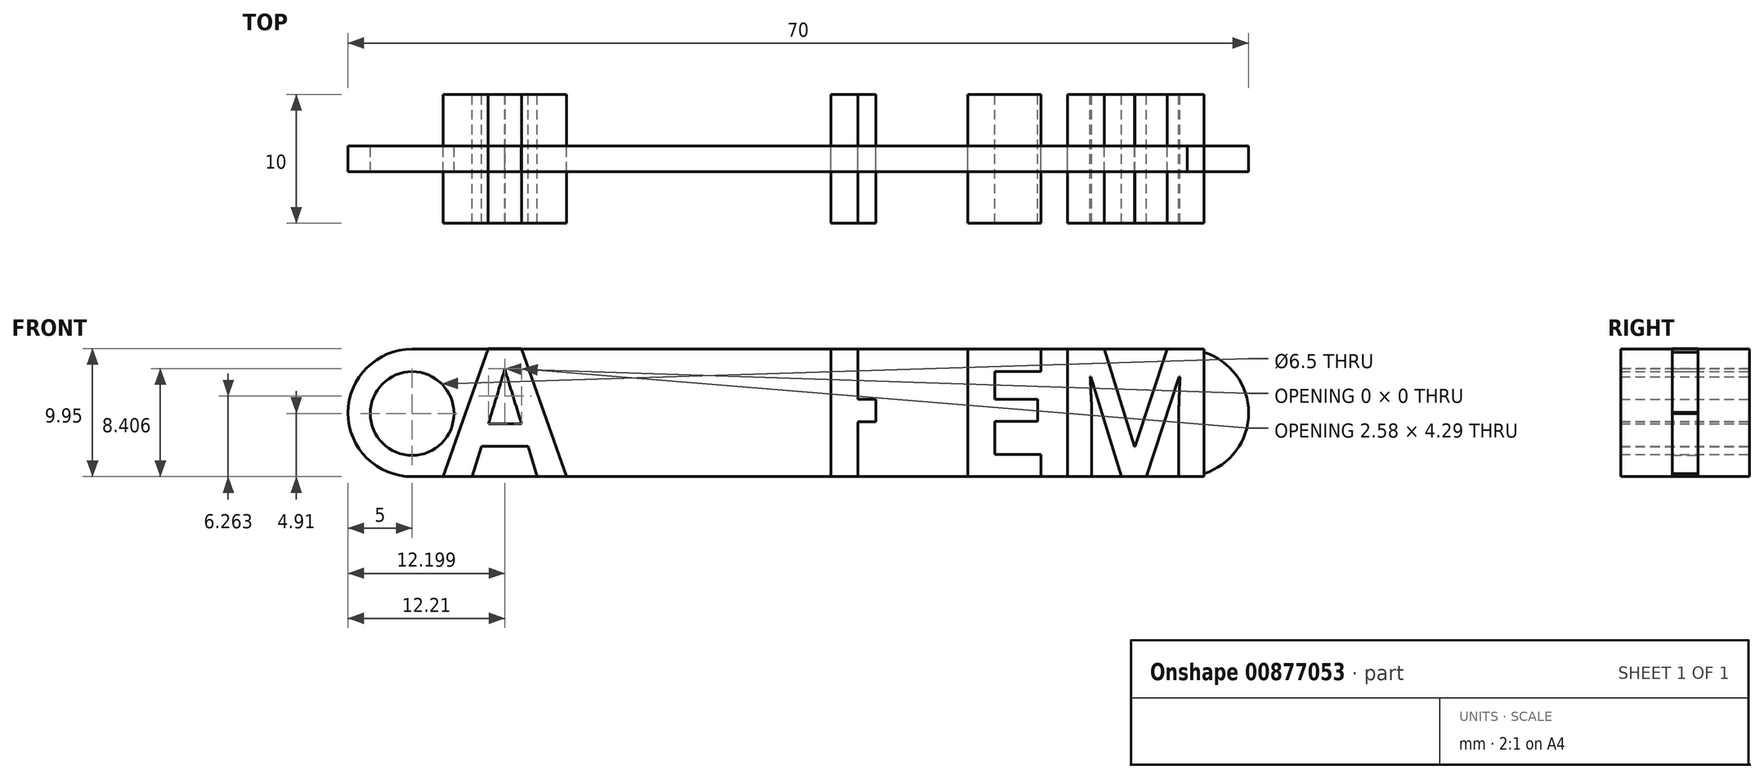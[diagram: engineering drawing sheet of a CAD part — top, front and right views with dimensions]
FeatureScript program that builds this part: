
annotation { "Feature Type Name" : "Feature", "Feature Type Description" : "" }
export const myFeature = defineFeature(function(context is Context, id is Id, definition is map)
    precondition{}
    {
        {
            var Q0;
            Q0=qCreatedBy(makeId("Front.planeOp"),FACE);
            var sketch = newSketch(context, id + "F0", { "sketchPlane" : qUnion([Q0])});
            skLineSegment(sketch, "E0.bottom", {"start": v(-30, 9.9) * mm, "end": v(30, 9.9) * mm});
            skLineSegment(sketch, "E0.top", {"start": v(-30, 0) * mm, "end": v(30, 0) * mm});
            skLineSegment(sketch, "E0.left", {"start": v(-35, 5) * mm, "end": v(-35, 4.9) * mm});
            skLineSegment(sketch, "E0.right", {"start": v(35, 5) * mm, "end": v(35, 4.9) * mm});
            skPoint(sketch, "E1.visualSharp", {"position": v(-35, 9.9) * mm});
            skArc(sketch, "E1.filletArc", {"start": v(-30, 9.9) * mm, "mid": v(-33.54, 8.45) * mm, "end": v(-35, 4.9) * mm});
            skPoint(sketch, "E2.visualSharp", {"position": v(-35, 0) * mm});
            skArc(sketch, "E2.filletArc", {"start": v(-35, 5) * mm, "mid": v(-33.54, 1.46) * mm, "end": v(-30, 0) * mm});
            skCircle(sketch, "E3", {"center": v(-30, 4.9) * mm, "radius": 3.25 * mm});
            skText(sketch, "E4", { "text": "ANTHEM\n", "fontName": "OpenSans-Bold.ttf"});
            skPoint(sketch, "E5", {"position": v(-24.08, 4.12) * mm});
            skPoint(sketch, "E6", {"position": v(-26.14, 4.12) * mm});
            skPoint(sketch, "E7", {"position": v(-22.8, 8.4) * mm});
            skPoint(sketch, "E8", {"position": v(-24.63, 8.4) * mm});
            skPoint(sketch, "E9", {"position": v(4.64, 6.03) * mm});
            skPoint(sketch, "E10", {"position": v(4.64, 4.27) * mm});
            skPoint(sketch, "E11", {"position": v(6.04, 6.03) * mm});
            skPoint(sketch, "E12", {"position": v(6.04, 4.27) * mm});
            skPoint(sketch, "E13", {"position": v(15.26, 6) * mm});
            skPoint(sketch, "E14", {"position": v(13.16, 6) * mm});
            skPoint(sketch, "E15", {"position": v(15.26, 4.29) * mm});
            skPoint(sketch, "E16", {"position": v(13.16, 4.29) * mm});
            skLineSegment(sketch, "E17", {"start": v(6.04, 4.27) * mm, "end": v(6.04, 6.03) * mm});
            skLineSegment(sketch, "E18", {"start": v(4.64, 4.27) * mm, "end": v(4.64, 6.03) * mm});
            skLineSegment(sketch, "E19", {"start": v(13.16, 6) * mm, "end": v(15.26, 6) * mm});
            skLineSegment(sketch, "E20", {"start": v(15.26, 8.18) * mm, "end": v(13.13, 8.18) * mm});
            skLineSegment(sketch, "E21", {"start": v(-26.14, 4.12) * mm, "end": v(-24.08, 4.12) * mm});
            skLineSegment(sketch, "E22", {"start": v(-22.8, 8.4) * mm, "end": v(-24.63, 8.4) * mm});
            skLineSegment(sketch, "E23", {"start": v(-22.8, 8.4) * mm, "end": v(-23.28, 9.99) * mm});
            skPoint(sketch, "E24", {"position": v(-21.52, 9.95) * mm});
            skPoint(sketch, "E25", {"position": v(-20.98, 8.4) * mm});
            skLineSegment(sketch, "E26", {"start": v(-20.98, 8.4) * mm, "end": v(-21.52, 9.95) * mm});
            skPoint(sketch, "E27.visualSharp", {"position": v(35, 9.9) * mm});
            skArc(sketch, "E27.filletArc", {"start": v(35, 4.9) * mm, "mid": v(33.54, 8.45) * mm, "end": v(30, 9.9) * mm});
            skPoint(sketch, "E28.visualSharp", {"position": v(35, 0) * mm});
            skArc(sketch, "E28.filletArc", {"start": v(30, 0) * mm, "mid": v(33.54, 1.46) * mm, "end": v(35, 5) * mm});
            const initialGuessF0  = {"E4": [-0.02759, 0, 1, 0, 0.00999]};
            skSetInitialGuess(sketch, initialGuessF0);
            skSolve(sketch);
        }
        {
            var Q0;
            Q0=makeQuery(id+"F0.imprint","IMPRINT",FACE,{"disambiguationData":[TD([[makeQuery(id+"F0.imprint","IMPRINT",EDGE,{"derivedFrom":sQuery(id+"F0.wireOp",EDGE,"E4.sketch_text.stroke-12")}),-1.0]])]});
            var Q1;
            Q1=makeQuery(id+"F0.imprint","IMPRINT",FACE,{"disambiguationData":[TD([[makeQuery(id+"F0.imprint","IMPRINT",EDGE,{"derivedFrom":sQuery(id+"F0.wireOp",EDGE,"E4.sketch_text.stroke-26")}),-1.0]])]});
            var Q2;
            Q2=makeQuery(id+"F0.imprint","IMPRINT",FACE,{"disambiguationData":[TD([[makeQuery(id+"F0.imprint","IMPRINT",EDGE,{"derivedFrom":sQuery(id+"F0.wireOp",EDGE,"E4.sketch_text.stroke-0")}),-1.0]])]});
            var Q3;
            {var subQ3=sQuery(id+"F0.wireOp",EDGE,"E4.sketch_text.stroke-37");Q3=makeQuery(id+"F0.imprint","IMPRINT",FACE,{"disambiguationData":[TD([[makeQuery(id+"F0.imprint","IMPRINT",EDGE,{"derivedFrom":subQ3}),-1.0]])]});}
            var Q4;
            Q4=makeQuery(id+"F0.imprint","IMPRINT",FACE,{"disambiguationData":[TD([[makeQuery(id+"F0.imprint","IMPRINT",EDGE,{"derivedFrom":sQuery(id+"F0.wireOp",EDGE,"E4.sketch_text.stroke-34")}),-1.0]])]});
            var Q5;
            {var subQ4=sQuery(id+"F0.wireOp",EDGE,"E4.sketch_text.stroke-46");Q5=makeQuery(id+"F0.imprint","IMPRINT",FACE,{"disambiguationData":[TD([[makeQuery(id+"F0.imprint","IMPRINT",EDGE,{"derivedFrom":subQ4}),-1.0]])]});}
            var Q6;
            {var subQ1=sQuery(id+"F0.wireOp",EDGE,"E4.sketch_text.stroke-48");Q6=makeQuery(id+"F0.imprint","IMPRINT",FACE,{"disambiguationData":[TD([[makeQuery(id+"F0.imprint","IMPRINT",EDGE,{"derivedFrom":subQ1}),-1.0]])]});}
            var Q7;
            Q7=makeQuery(id+"F0.imprint","IMPRINT",FACE,{"disambiguationData":[TD([[makeQuery(id+"F0.imprint","IMPRINT",EDGE,{"derivedFrom":sQuery(id+"F0.wireOp",EDGE,"E4.sketch_text.stroke-58")}),-1.0]])]});
            var Q8;
            {var subQ0=sQuery(id+"F0.wireOp",EDGE,"E4.sketch_text.stroke-70");var subQ1=sQuery(id+"F0.wireOp",EDGE,"E4.sketch_text.stroke-69");var subQ2=makeQuery(id+"F0.imprint","INTERSECT",VERTEX,{"derivedFrom":[subQ1,subQ0]});Q8=makeQuery(id+"F0.imprint","IMPRINT",FACE,{"disambiguationData":[TD([[makeQuery(id+"F0.imprint","IMPRINT",EDGE,{"disambiguationData":[TD([[subQ2,1.0]])],"derivedFrom":subQ1}),-1.0]])]});}
            var Q9;
            {var subQ0=sQuery(id+"F0.wireOp",EDGE,"E4.sketch_text.stroke-69");var subQ1=sQuery(id+"F0.wireOp",EDGE,"E4.sketch_text.stroke-68");var subQ2=makeQuery(id+"F0.imprint","INTERSECT",VERTEX,{"derivedFrom":[subQ1,subQ0]});Q9=makeQuery(id+"F0.imprint","IMPRINT",FACE,{"disambiguationData":[TD([[makeQuery(id+"F0.imprint","IMPRINT",EDGE,{"disambiguationData":[TD([[subQ2,1.0]])],"derivedFrom":subQ1}),-1.0]])]});}
            extrude(context, id + "F1", {"entities" : qUnion([Q0, Q1, Q2, Q3, Q4, Q5, Q6, Q7, Q8, Q9]), "endBound" : BoundingType.SYMMETRIC, "depth" : 10 * mm, "offsetDistance" : 25 * mm});
        }
        {
            var Q0;
            Q0 = qSketchRegion(id + "F0", true);
            var Q1;
            {var subQ5=sQuery(id+"F0.wireOp",EDGE,"E4.sketch_text.stroke-8");Q1=makeQuery(id+"F0.imprint","IMPRINT",FACE,{"disambiguationData":[TD([[makeQuery(id+"F0.imprint","IMPRINT",EDGE,{"derivedFrom":subQ5}),1.0]])]});}
            var Q2;
            {var subQ0=sQuery(id+"F0.wireOp",EDGE,"E18");var subQ1=sQuery(id+"F0.wireOp",EDGE,"E4.sketch_text.stroke-36");var subQ2=makeQuery(id+"F0.imprint","INTERSECT",VERTEX,{"derivedFrom":[subQ1,subQ0]});Q2=makeQuery(id+"F0.imprint","IMPRINT",FACE,{"disambiguationData":[TD([[makeQuery(id+"F0.imprint","IMPRINT",EDGE,{"disambiguationData":[TD([[subQ2,1.0]])],"derivedFrom":subQ1}),-1.0]])]});}
            var Q3;
            {var subQ0=sQuery(id+"F0.wireOp",EDGE,"E19");Q3=makeQuery(id+"F0.imprint","IMPRINT",FACE,{"disambiguationData":[TD([[makeQuery(id+"F0.imprint","IMPRINT",EDGE,{"derivedFrom":subQ0}),1.0]])]});}
            extrude(context, id + "F2", {"entities" : qUnion([Q0, Q1, Q2, Q3]), "endBound" : BoundingType.SYMMETRIC, "depth" : 2 * mm, "offsetDistance" : 25 * mm});
        }
    });
